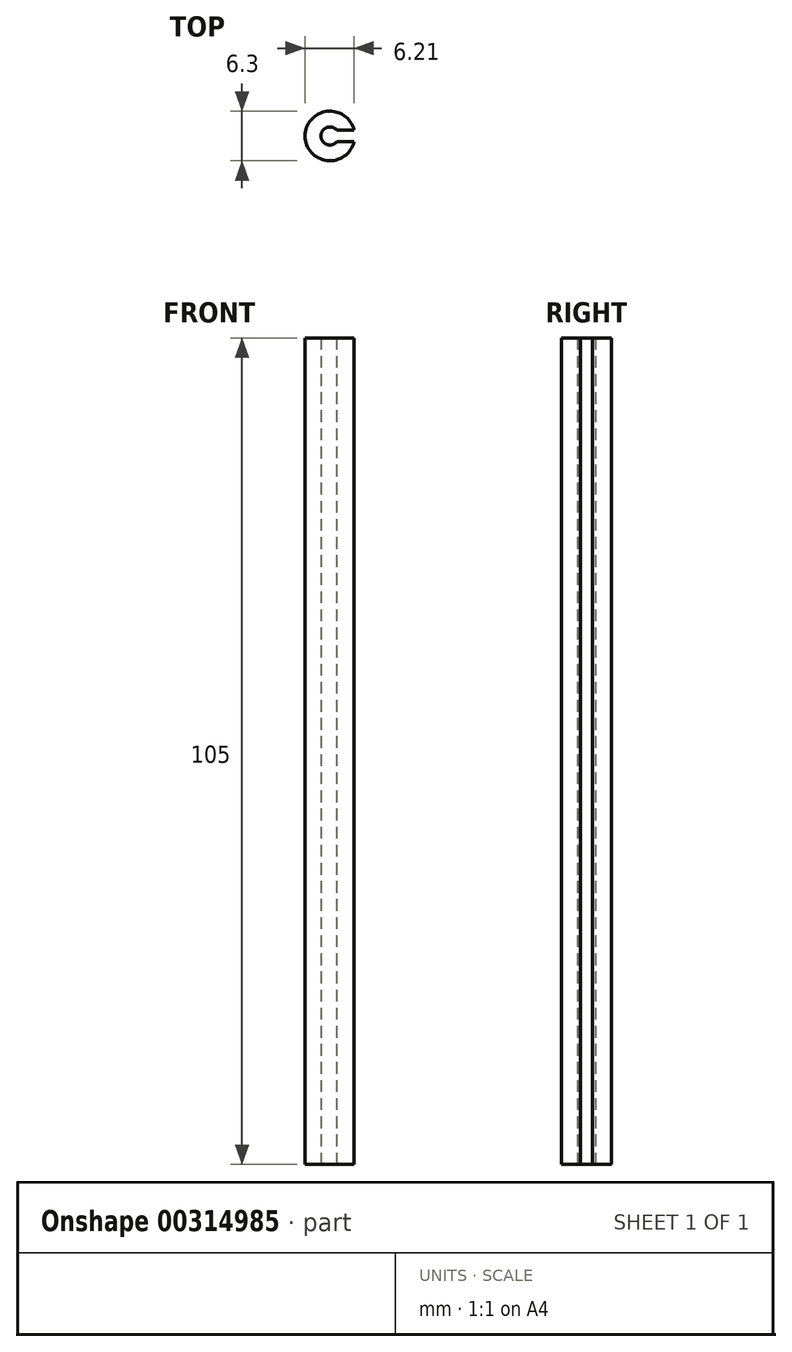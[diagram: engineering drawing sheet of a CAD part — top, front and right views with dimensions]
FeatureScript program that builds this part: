
annotation { "Feature Type Name" : "Feature", "Feature Type Description" : "" }
export const myFeature = defineFeature(function(context is Context, id is Id, definition is map)
    precondition{}
    {
        {
            var Q0;
            Q0=qCreatedBy(makeId("Top.planeOp"),FACE);
            var sketch = newSketch(context, id + "F0", { "sketchPlane" : qUnion([Q0])});
            skCircle(sketch, "E0", {"center": v(0, 0) * mm, "radius": 1.15 * mm});
            skCircle(sketch, "E1.0", {"center": v(0, 0) * mm, "radius": 3.15 * mm});
            skSolve(sketch);
        }
        {
            var Q0;
            Q0=makeQuery(id+"F0.imprint","IMPRINT",FACE,{"disambiguationData":[TD([[makeQuery(id+"F0.imprint","IMPRINT",EDGE,{"derivedFrom":sQuery(id+"F0.wireOp",EDGE,"E0")}),-1.0]])]});
            extrude(context, id + "F1", {"entities" : qUnion([Q0]), "depth" : 105 * mm});
        }
        {
            var Q0;
            Q0=makeQuery(id+"F1.opExtrude","CAP_FACE",FACE,{"disambiguationData":[OSD([sQuery(id+"F0.wireOp",EDGE,"E0"),sQuery(id+"F0.wireOp",EDGE,"E1.0")])],"isStart":false});
            var sketch = newSketch(context, id + "F2", { "sketchPlane" : qUnion([Q0])});
            skLineSegment(sketch, "E2", {"start": v(-0.87, -0.75) * mm, "end": v(3.06, -0.75) * mm});
            skLineSegment(sketch, "E3", {"start": v(-0.87, 0.75) * mm, "end": v(3.06, 0.75) * mm});
            skLineSegment(sketch, "E4", {"start": v(0, 0) * mm, "end": v(3.15, 0) * mm, "construction": true});
            skLineSegment(sketch, "E5", {"start": v(1.57, 0) * mm, "end": v(1.57, 0.75) * mm, "construction": true});
            skPoint(sketch, "E5.endSnap0", {"position": v(1.1, 0.75) * mm});
            skLineSegment(sketch, "E6", {"start": v(1.58, 0) * mm, "end": v(1.58, -0.75) * mm, "construction": true});
            skLineSegment(sketch, "E7", {"start": v(-0.87, 0.75) * mm, "end": v(-0.87, -0.75) * mm});
            skSolve(sketch);
        }
        {
            var Q0;
            {var subQ0=sQuery(id+"F2.wireOp",EDGE,"E2");var subQ1=makeQuery(id+"F1.opExtrude","CAP_EDGE",EDGE,{"disambiguationData":[OSD([sQuery(id+"F0.wireOp",EDGE,"E1.0")])],"isStart":false});var subQ2=makeQuery(id+"F2.imprint","INTERSECT",VERTEX,{"derivedFrom":[subQ1,subQ0]});Q0=makeQuery(id+"F2.imprint","IMPRINT",FACE,{"disambiguationData":[TD([[makeQuery(id+"F2.imprint","IMPRINT",EDGE,{"disambiguationData":[TD([[subQ2,1.0]])],"derivedFrom":subQ0}),1.0]])]});}
            extrude(context, id + "F3", {"entities" : qUnion([Q0]), "operationType" : NewBodyOperationType.REMOVE, "endBound" : BoundingType.THROUGH_ALL, "oppositeDirection" : true, "depth" : 25 * mm});
        }
    });
